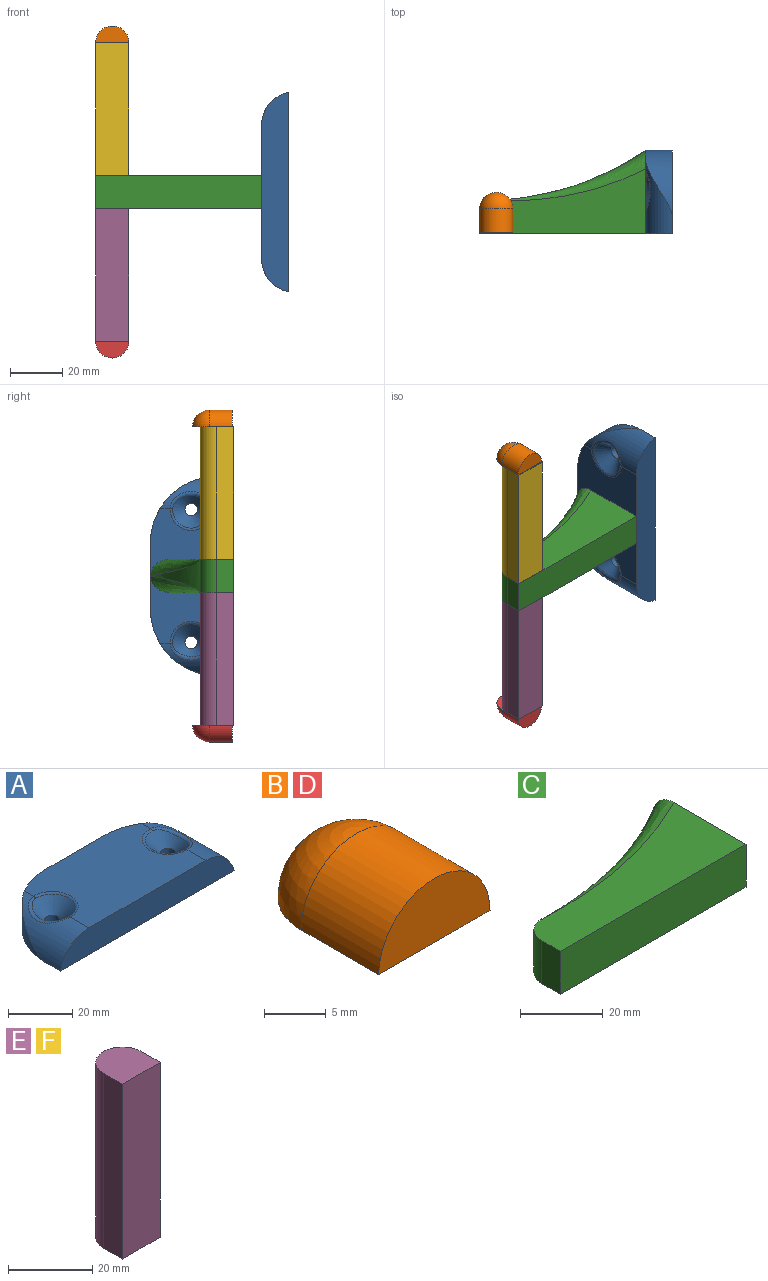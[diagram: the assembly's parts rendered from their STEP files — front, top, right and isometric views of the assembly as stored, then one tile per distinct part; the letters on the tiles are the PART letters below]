
ASSEMBLY  parts=6 mates=5
PART A: 16 faces, bbox 76.2x31.8x10.2 mm
  f0: plane 76.2x10.16mm, normal (0,-1,0), area 710.6mm2, adj f4,f5,f10,f11
  f1: cylinder r=2.38mm len=5.08mm, axis (0,0,-1), area 76mm2, adj f5,f6
  f2: plane 25.4x10.16mm, normal (0,1,0), area 258.1mm2, adj f4,f5,f8,f9
  f3: cylinder r=2.38mm len=5.08mm, axis (0,0,-1), area 76mm2, adj f5,f7
  f4: plane 51.31x31.75mm, normal (0,0,1), area 1390.8mm2, adj f0,f2,f8,f9,f10,f11,f12,f14
  f5: plane 76.2x31.75mm, normal (0,0,-1), area 2106.8mm2, adj f0,f1,f2,f3,f8,f9,f10,f11
  f6: cone r=2.38mm half-angle=45deg, axis (0,0,1), area 171.7mm2, adj f1,f12,f13
  f7: cone r=2.38mm half-angle=45deg, axis (0,0,1), area 171.7mm2, adj f3,f14,f15
  f8: cylinder r=25.4mm len=25.4mm, axis (0,0,1), area 290.1mm2, adj f2,f4,f5,f10
  f9: cylinder r=25.4mm len=25.4mm, axis (0,0,-1), area 290.1mm2, adj f2,f4,f5,f11
  f10: cylinder r=12.7mm len=28.2mm, axis (0,1,0), area 258.6mm2, adj f0,f4,f5,f8,f15
  f11: cylinder r=12.7mm len=28.2mm, axis (0,1,0), area 258.6mm2, adj f0,f4,f5,f9,f13
  f12: torus R=7.99mm, axis (0,0,1), area 24mm2, adj f4,f6,f13
  f13: bspline ~15.98x7.85mm, area 29.1mm2, adj f6,f11,f12
  f14: torus R=7.99mm, axis (0,0,1), area 24mm2, adj f4,f7,f15
  f15: bspline ~15.98x7.85mm, area 29.1mm2, adj f7,f10,f14
PART B: 4 faces, bbox 12.7x15.2x6.4 mm
  f0: plane 12.7x6.35mm, normal (0,-1,0), area 63.3mm2, adj f1,f2
  f1: plane 15.24x12.7mm, normal (0,0,-1), area 176.2mm2, adj f0,f2,f3
  f2: cylinder r=6.35mm len=12.7mm, axis (0,1,0), area 177.3mm2, adj f0,f1,f3
  f3: sphere r=6.35mm, area 126.7mm2, adj f1,f2
PART C: 9 faces, bbox 74x37.6x16.8 mm
  f0: plane 63.5x12.7mm, normal (0,-1,0), area 806.5mm2, adj f1,f3,f4,f5
  f1: plane 33.16x14.11mm, normal (1,0,0), area 383.3mm2, adj f0,f4,f5,f7,f8
  f2: cylinder r=109.43mm len=57.4mm, axis (0,0,-1), area 389mm2, adj f6,f7,f8
  f3: plane 12.7x6.43mm, normal (-1,0,0), area 81.6mm2, adj f0,f4,f5,f6
  f4: plane 67.63x28.76mm, normal (0,0,1), area 989.3mm2, adj f0,f1,f3,f6,f7
  f5: plane 67.63x28.76mm, normal (0,0,-1), area 989.3mm2, adj f0,f1,f3,f6,f8
  f6: cylinder r=6.35mm len=12.7mm, axis (0,0,-1), area 123.5mm2, adj f2,f3,f4,f5
  f7: bspline ~63.82x21.43mm, area 200.4mm2, adj f1,f2,f4
  f8: bspline ~63.82x21.43mm, area 200.4mm2, adj f1,f2,f5
PART D: same geometry as B
PART E: 6 faces, bbox 12.7x12.7x50.8 mm
  f0: cylinder r=6.35mm len=50.8mm, axis (0,0,-1), area 1013.4mm2, adj f1,f3,f4,f5
  f1: plane 50.8x6.35mm, normal (-1,0,0), area 322.6mm2, adj f0,f2,f4,f5
  f2: plane 50.8x12.7mm, normal (0,-1,0), area 645.2mm2, adj f1,f3,f4,f5
  f3: plane 50.8x6.35mm, normal (1,0,0), area 322.6mm2, adj f0,f2,f4,f5
  f4: plane 12.7x12.7mm, normal (0,0,1), area 144mm2, adj f0,f1,f2,f3
  f5: plane 12.7x12.7mm, normal (0,0,-1), area 144mm2, adj f0,f1,f2,f3
PART F: same geometry as E
PLACE A rot(axis=(0,-1,0),90deg) t=(67.31,12.95,77.47)mm
PLACE B t=(0,6.03,134.62)mm
PLACE C t=(57.15,-3.25,71.12)mm
PLACE D rot(axis=(0,1,0),180deg) t=(0,6.03,20.32)mm
PLACE E t=(0,3.18,20.32)mm
PLACE F t=(0,3.18,83.82)mm
MATE planar F.f0 <-> C.f6  axis (0,0,-1) through (0,3.18,83.82)mm
MATE planar F.f4 <-> B.f1  axis (0,0,1) through (0,-3.17,134.62)mm
MATE planar E.f0 <-> C.f6  axis (0,0,1) through (0,3.18,71.12)mm
MATE planar A.f4 <-> C.f1  axis (-1,0,0) through (57.15,12.26,77.47)mm
MATE planar D.f1 <-> E.f5  axis (0,0,1) through (0,-2.86,20.32)mm
